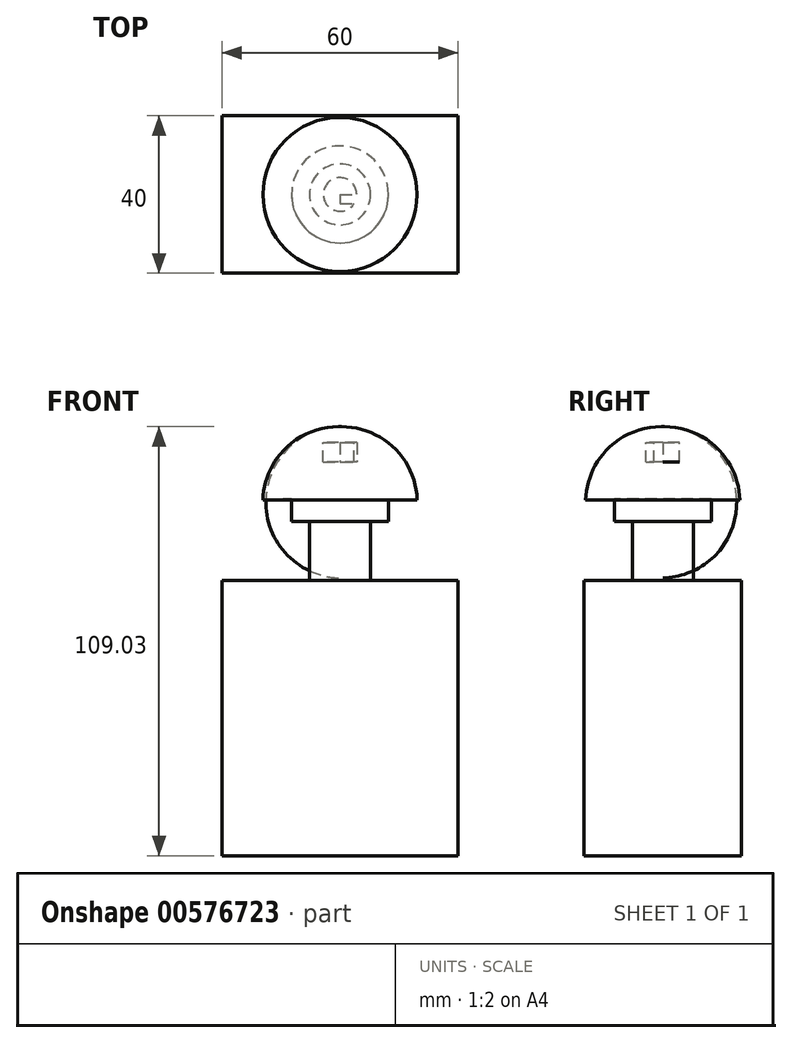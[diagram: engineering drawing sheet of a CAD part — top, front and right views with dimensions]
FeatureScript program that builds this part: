
annotation { "Feature Type Name" : "Feature", "Feature Type Description" : "" }
export const myFeature = defineFeature(function(context is Context, id is Id, definition is map)
    precondition{}
    {
        {
            var Q0;
            Q0=qCreatedBy(makeId("Top.planeOp"),FACE);
            var sketch = newSketch(context, id + "F0", { "sketchPlane" : qUnion([Q0])});
            skLineSegment(sketch, "E0.bottom", {"start": v(-46.06, 29.85) * mm, "end": v(13.94, 29.85) * mm});
            skLineSegment(sketch, "E0.top", {"start": v(-46.06, -10.15) * mm, "end": v(13.94, -10.15) * mm});
            skLineSegment(sketch, "E0.left", {"start": v(-46.06, 29.85) * mm, "end": v(-46.06, -10.15) * mm});
            skLineSegment(sketch, "E0.right", {"start": v(13.94, 29.85) * mm, "end": v(13.94, -10.15) * mm});
            skSolve(sketch);
        }
        {
            var Q0;
            Q0 = qSketchRegion(id + "F0", true);
            extrude(context, id + "F1", {"entities" : qUnion([Q0]), "depth" : 70 * mm, "offsetDistance" : 25 * mm});
        }
        {
            var Q0;
            Q0=makeQuery(id+"F1.opExtrude","CAP_FACE",FACE,{"disambiguationData":[OSD([sQuery(id+"F0.wireOp",EDGE,"E0.bottom"),sQuery(id+"F0.wireOp",EDGE,"E0.top"),sQuery(id+"F0.wireOp",EDGE,"E0.left"),sQuery(id+"F0.wireOp",EDGE,"E0.right")])],"isStart":false});
            var sketch = newSketch(context, id + "F2", { "sketchPlane" : qUnion([Q0])});
            skCircle(sketch, "E1", {"center": v(-16.06, 9.85) * mm, "radius": 7.75 * mm});
            skPoint(sketch, "E2.orphan", {"position": v(-46.06, -10.15) * mm});
            skPoint(sketch, "E3.orphan", {"position": v(13.94, 29.85) * mm});
            skSolve(sketch);
        }
        {
            var Q0;
            Q0 = qSketchRegion(id + "F2", true);
            extrude(context, id + "F3", {"entities" : qUnion([Q0]), "operationType" : NewBodyOperationType.ADD, "depth" : 15 * mm, "offsetDistance" : 25 * mm});
        }
        {
            var Q0;
            Q0=makeQuery(id+"F3.opExtrude","CAP_FACE",FACE,{"disambiguationData":[OSD([sQuery(id+"F2.wireOp",EDGE,"E1")])],"isStart":false});
            var sketch = newSketch(context, id + "F4", { "sketchPlane" : qUnion([Q0])});
            skCircle(sketch, "E4", {"center": v(-16.06, 9.85) * mm, "radius": 12.32 * mm});
            skSolve(sketch);
        }
        {
            var Q0;
            Q0 = qSketchRegion(id + "F4", true);
            extrude(context, id + "F5", {"entities" : qUnion([Q0]), "operationType" : NewBodyOperationType.ADD, "depth" : 15 * mm, "offsetDistance" : 25 * mm});
        }
        {
            var Q0;
            Q0=makeQuery(id+"F5.opExtrude","CAP_FACE",FACE,{"disambiguationData":[OSD([sQuery(id+"F4.wireOp",EDGE,"E4")])],"isStart":false});
            var sketch = newSketch(context, id + "F6", { "sketchPlane" : qUnion([Q0])});
            skLineSegment(sketch, "E5.bottom", {"start": v(-16.06, 9.85) * mm, "end": v(-11.8, 9.85) * mm});
            skLineSegment(sketch, "E5.top", {"start": v(-16.06, 7.56) * mm, "end": v(-11.8, 7.56) * mm});
            skLineSegment(sketch, "E5.left", {"start": v(-16.06, 9.85) * mm, "end": v(-16.06, 7.56) * mm});
            skLineSegment(sketch, "E5.right", {"start": v(-11.8, 9.85) * mm, "end": v(-11.8, 7.56) * mm});
            skSolve(sketch);
        }
        {
            var Q0;
            Q0 = qSketchRegion(id + "F6", true);
            extrude(context, id + "F7", {"entities" : qUnion([Q0]), "operationType" : NewBodyOperationType.ADD, "depth" : 5 * mm, "offsetDistance" : 25 * mm});
        }
        {
            var Q0;
            Q0=makeQuery(id+"F7.opExtrude","SWEPT_FACE",FACE,{"disambiguationData":[OSD([sQuery(id+"F6.wireOp",EDGE,"E5.bottom")])]});
            var sketch = newSketch(context, id + "F8", { "sketchPlane" : qUnion([Q0])});
            skLineSegment(sketch, "E6", {"start": v(16.06, 100) * mm, "end": v(16.06, 109.03) * mm});
            skLineSegment(sketch, "E7", {"start": v(16.06, 100) * mm, "end": v(16.06, 90.97) * mm});
            skArc(sketch, "E8", {"start": v(16.06, 109.03) * mm, "mid": v(2.46, 103.76) * mm, "end": v(-3.53, 90.46) * mm});
            skLineSegment(sketch, "E9", {"start": v(-3.53, 90.46) * mm, "end": v(16.06, 90.97) * mm});
            skSolve(sketch);
        }
        {
            var Q0;
            Q0=makeQuery(id+"F8.imprint","IMPRINT",FACE,{"disambiguationData":[TD([[makeQuery(id+"F8.imprint","IMPRINT",EDGE,{"derivedFrom":sQuery(id+"F8.wireOp",EDGE,"E7")}),-1.0]])]});
            var Q1;
            Q1=sQuery(id+"F8.wireOp",EDGE,"E7");
            revolve(context, id + "F9", {"operationType" : NewBodyOperationType.ADD, "entities" : qUnion([Q0]), "axis" : qUnion([Q1]), "revolveType" : RevolveType.FULL});
        }
    });
